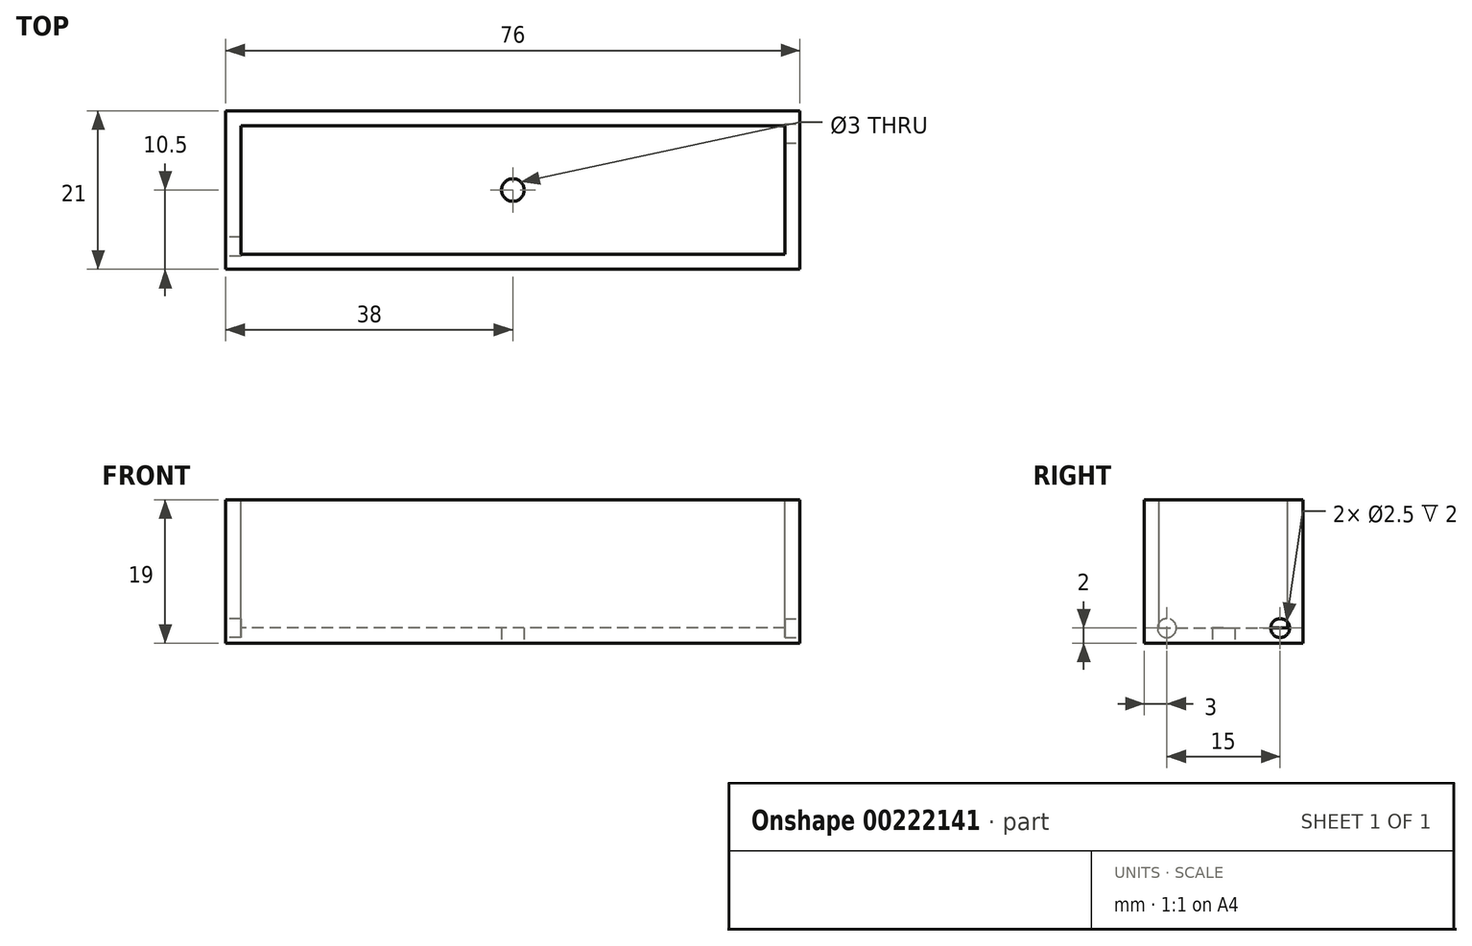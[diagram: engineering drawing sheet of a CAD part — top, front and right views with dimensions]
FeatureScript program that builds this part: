
annotation { "Feature Type Name" : "Feature", "Feature Type Description" : "" }
export const myFeature = defineFeature(function(context is Context, id is Id, definition is map)
    precondition{}
    {
        {
            var Q0;
            Q0=qCreatedBy(makeId("Top.planeOp"),FACE);
            var sketch = newSketch(context, id + "F0", { "sketchPlane" : qUnion([Q0])});
            skLineSegment(sketch, "E0.bottom", {"start": v(38, -10.5) * mm, "end": v(-38, -10.5) * mm});
            skLineSegment(sketch, "E0.top", {"start": v(38, 10.5) * mm, "end": v(-38, 10.5) * mm});
            skLineSegment(sketch, "E0.left", {"start": v(38, -10.5) * mm, "end": v(38, 10.5) * mm});
            skLineSegment(sketch, "E0.right", {"start": v(-38, -10.5) * mm, "end": v(-38, 10.5) * mm});
            skPoint(sketch, "E0.middle", {"position": v(0, 0) * mm});
            skSolve(sketch);
        }
        {
            var Q0;
            Q0 = qSketchRegion(id + "F0", true);
            extrude(context, id + "F1", {"entities" : qUnion([Q0]), "depth" : 19 * mm});
        }
        {
            var Q0;
            Q0=makeQuery(id+"F1.opExtrude","CAP_FACE",FACE,{"disambiguationData":[OSD([sQuery(id+"F0.wireOp",EDGE,"E0.bottom"),sQuery(id+"F0.wireOp",EDGE,"E0.top"),sQuery(id+"F0.wireOp",EDGE,"E0.left"),sQuery(id+"F0.wireOp",EDGE,"E0.right")])],"isStart":false});
            var sketch = newSketch(context, id + "F2", { "sketchPlane" : qUnion([Q0])});
            skLineSegment(sketch, "E1.bottom", {"start": v(36, -8.5) * mm, "end": v(-36, -8.5) * mm});
            skLineSegment(sketch, "E1.top", {"start": v(36, 8.5) * mm, "end": v(-36, 8.5) * mm});
            skLineSegment(sketch, "E1.left", {"start": v(36, -8.5) * mm, "end": v(36, 8.5) * mm});
            skLineSegment(sketch, "E1.right", {"start": v(-36, -8.5) * mm, "end": v(-36, 8.5) * mm});
            skPoint(sketch, "E1.middle", {"position": v(0, 0) * mm});
            skSolve(sketch);
        }
        {
            var Q0;
            Q0 = qSketchRegion(id + "F2", true);
            extrude(context, id + "F3", {"entities" : qUnion([Q0]), "operationType" : NewBodyOperationType.REMOVE, "oppositeDirection" : true, "depth" : 17 * mm});
        }
        {
            var Q0;
            Q0=makeQuery(id+"F1.opExtrude","CAP_FACE",FACE,{"disambiguationData":[OSD([sQuery(id+"F0.wireOp",EDGE,"E0.bottom"),sQuery(id+"F0.wireOp",EDGE,"E0.top"),sQuery(id+"F0.wireOp",EDGE,"E0.left"),sQuery(id+"F0.wireOp",EDGE,"E0.right")])],"isStart":true});
            var sketch = newSketch(context, id + "F4", { "sketchPlane" : qUnion([Q0])});
            skCircle(sketch, "E2", {"center": v(0, 0) * mm, "radius": 1.5 * mm});
            skSolve(sketch);
        }
        {
            var Q0;
            Q0 = qSketchRegion(id + "F4", true);
            extrude(context, id + "F5", {"entities" : qUnion([Q0]), "operationType" : NewBodyOperationType.REMOVE, "endBound" : BoundingType.THROUGH_ALL, "oppositeDirection" : true, "depth" : 25 * mm});
        }
        {
            var Q0;
            Q0=makeQuery(id+"F1.opExtrude","SWEPT_FACE",FACE,{"disambiguationData":[OSD([sQuery(id+"F0.wireOp",EDGE,"E0.right")])]});
            var sketch = newSketch(context, id + "F6", { "sketchPlane" : qUnion([Q0])});
            skLineSegment(sketch, "E3.bottom", {"start": v(10.5, 0) * mm, "end": v(7.5, 0) * mm, "construction": true});
            skLineSegment(sketch, "E3.top", {"start": v(10.5, 2) * mm, "end": v(7.5, 2) * mm, "construction": true});
            skLineSegment(sketch, "E3.left", {"start": v(10.5, 0) * mm, "end": v(10.5, 2) * mm, "construction": true});
            skLineSegment(sketch, "E3.right", {"start": v(7.5, 0) * mm, "end": v(7.5, 2) * mm, "construction": true});
            skCircle(sketch, "E4", {"center": v(7.5, 2) * mm, "radius": 1.25 * mm});
            skPoint(sketch, "E5.centerSnap0", {"position": v(9, 0) * mm});
            skSolve(sketch);
        }
        {
            var Q0;
            Q0 = qSketchRegion(id + "F6", true);
            extrude(context, id + "F7", {"entities" : qUnion([Q0]), "operationType" : NewBodyOperationType.REMOVE, "oppositeDirection" : true, "depth" : 2 * mm});
        }
        {
            var Q0;
            Q0=makeQuery(id+"F1.opExtrude","SWEPT_FACE",FACE,{"disambiguationData":[OSD([sQuery(id+"F0.wireOp",EDGE,"E0.left")])]});
            var sketch = newSketch(context, id + "F8", { "sketchPlane" : qUnion([Q0])});
            skLineSegment(sketch, "E6.bottom", {"start": v(10.5, 0) * mm, "end": v(7.5, 0) * mm, "construction": true});
            skLineSegment(sketch, "E6.top", {"start": v(10.5, 2) * mm, "end": v(7.5, 2) * mm});
            skLineSegment(sketch, "E6.left", {"start": v(10.5, 0) * mm, "end": v(10.5, 2) * mm, "construction": true});
            skLineSegment(sketch, "E6.right", {"start": v(7.5, 0) * mm, "end": v(7.5, 2) * mm});
            skCircle(sketch, "E7", {"center": v(7.5, 2) * mm, "radius": 1.25 * mm});
            skSolve(sketch);
        }
        {
            var Q0;
            Q0 = qSketchRegion(id + "F8", true);
            extrude(context, id + "F9", {"entities" : qUnion([Q0]), "operationType" : NewBodyOperationType.REMOVE, "oppositeDirection" : true, "depth" : 2 * mm});
        }
    });
